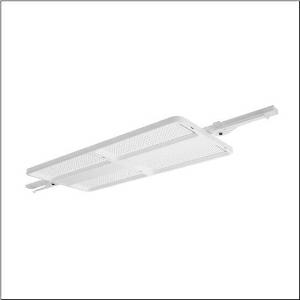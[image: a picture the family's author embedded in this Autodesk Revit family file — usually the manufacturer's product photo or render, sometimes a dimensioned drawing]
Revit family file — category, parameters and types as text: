
# Revit family: highbay_21_fur_modario_r__tragschiene_maxi_52hn12db3lma_0d32
name_source: partatom
category: Lighting Fixtures
units: mm (PartAtom-declared; Revit-internal decimal feet)

## family parameters
Cut with Voids When Loaded = No
Host = Face
Light Source = No
Part Type = Normal
Room Calculation Point = No
Round Connector Dimension = Use Diameter
Shared = No

## types (1)
- --- (1 x LED, 3880 lm, 22.6 W, 3000K)
    Apparent Load = 23 VA
    CIE Flux Codes = 90 98 100 100 100
    Color Rendering = 80
    Color Temperature = 3000K
    Default Elevation = 1800 mm
    Description = high bay luminaire Highbay 21 for Modario® trunking rail maxi; direct symmetric wide distribution, light control with lens of PMMA; UGR ≤ 22 (X = 4H | Y = 8H | S = 0.25H | reflection values 70/50/20); luminous flux: 25.590lm; light colour: 830, colour temperature: 3000K, MacAdam ≤ 3 SDCM (initial), colour rendering: CRI > 80; luminous efficacy: 177,7lm/W; rated service life: 75.000h (L80/B50) at AT= ta max; control: DALI 2; luminaire connection: plug, 5-pole, with phase selectionmains connection: 230..240V, AC 50/60Hz; connected load: 144W; protection rating (complete): IP64; insulation class (complete): insulation class I (protective earthing); protection symbol: D; impact resistance: IK07; certification: CE, ENEC, VDE, UKCA; internal wiring halogen-free; luminaire corresponds to IFS (International Featured Standards) requirements for safety and quality in the food industry; LABS conformity tested according to VDMA 24364:2018-05; housing frame of high-performance plastic PA6, matt traffic white (RAL 9016); cover of PMMA; fixing on rail side of steel, galvanised, white; blank cover of PC, traffic white (RAL 9016); dimension (LxWxH): 1.496 x 442 x 72mm; permissible operating ambient temperature: -40..+55°C (reducing of maximum allowable ambient temperature of 5°C with ceiling mounting); packaging unit: 1 piece
    Height = 72 mm  [stored 0.23622 ft]
    Lamp = 1 x LED
    Lamp Light Flux = 3880 lm
    Lamp Power = 22.6 W
    Lamp count = 1
    Length = 946 mm
    Luminous efficacy = 172 lm/W
    Manufacturer = Siteco
    ModVariant = No
    Model = 52HN12DB3LMA
    Mounting Place = Ceiling
    Mounting Type = Pendant
    Number of Poles = 1
    OnlyDefault = Yes
    Power Factor = 1
    Product Name = Highbay 21 für Modario® Tragschiene maxi
    Product group = high bay luminaire
    ProductGroupID = 901
    Protection Class = Protection class I
    Protection Degree = IP 64
    RLX_Detail_Level = 1
    RLX_Emergency_Light_Flux = 0 lm
    RLX_Emergency_Type = 0
    RLX_Emergency_Type_DB = No
    RlxData = <blob elided: 127469 chars, md5=26c3a669>
    Socket = socket
    Standby Power = 0 W
    System Light Flux = 3880 lm
    System Power = 23 W
    Type Comments = : DC mode (central or group accumulator) initial emergency light level
    Type Image = l_1363248.jpg
    URL = http://relux.com
    VarID = @adj_002567
    Voltage = 0 V
    Weight = 0.00 kg
    Width = 442 mm

note: [stored X ft] marks values corroborated as IEEE doubles in the binary element streams (Revit-internal decimal feet)

## geometry (parser evidence)
native form markers: Blend x4, Sweep x11
no freeform markers — native parametric forms only
